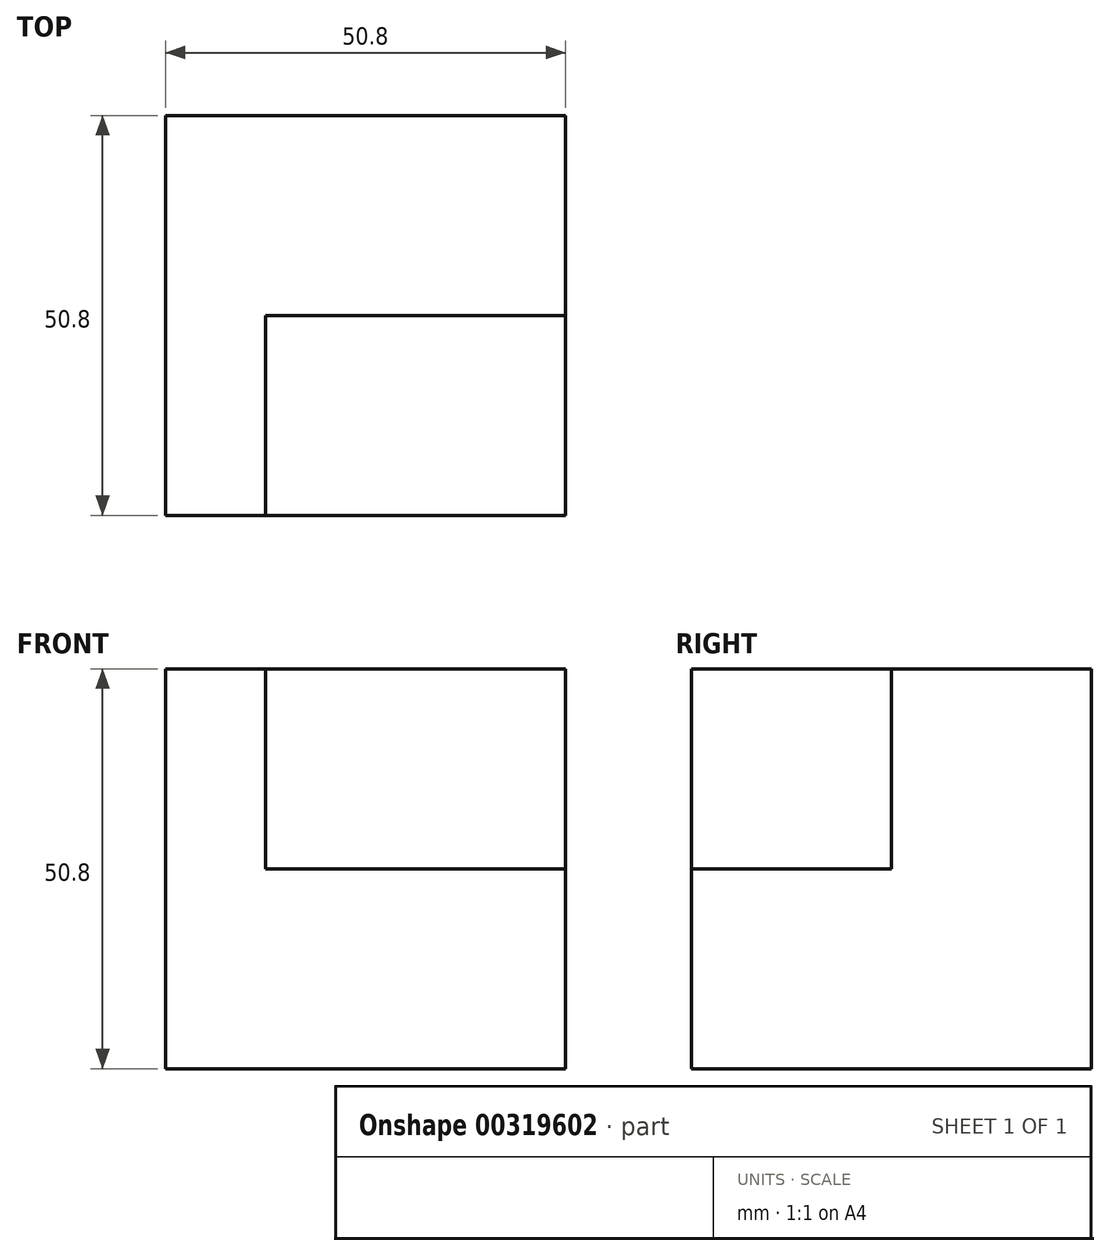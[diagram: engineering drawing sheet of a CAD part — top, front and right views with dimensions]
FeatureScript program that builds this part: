
annotation { "Feature Type Name" : "Feature", "Feature Type Description" : "" }
export const myFeature = defineFeature(function(context is Context, id is Id, definition is map)
    precondition{}
    {
        {
            var Q0;
            Q0=qCreatedBy(makeId("Front.planeOp"),FACE);
            var sketch = newSketch(context, id + "F0", { "sketchPlane" : qUnion([Q0])});
            skLineSegment(sketch, "E0.bottom", {"start": v(-36.56, 56.22) * mm, "end": v(14.24, 56.22) * mm});
            skLineSegment(sketch, "E0.top", {"start": v(-36.56, 5.42) * mm, "end": v(14.24, 5.42) * mm});
            skLineSegment(sketch, "E0.left", {"start": v(-36.56, 56.22) * mm, "end": v(-36.56, 5.42) * mm});
            skLineSegment(sketch, "E0.right", {"start": v(14.24, 56.22) * mm, "end": v(14.24, 5.42) * mm});
            skSolve(sketch);
        }
        {
            var Q0;
            Q0=makeQuery(id+"F0.imprint","IMPRINT",FACE,{"disambiguationData":[TD([[makeQuery(id+"F0.imprint","IMPRINT",EDGE,{"derivedFrom":sQuery(id+"F0.wireOp",EDGE,"E0.bottom")}),-1.0]])]});
            extrude(context, id + "F1", {"entities" : qUnion([Q0]), "depth" : 50.8 * mm});
        }
        {
            var Q0;
            Q0=makeQuery(id+"F1.opExtrude","CAP_FACE",FACE,{"disambiguationData":[OSD([sQuery(id+"F0.wireOp",EDGE,"E0.bottom"),sQuery(id+"F0.wireOp",EDGE,"E0.top"),sQuery(id+"F0.wireOp",EDGE,"E0.left"),sQuery(id+"F0.wireOp",EDGE,"E0.right")])],"isStart":false});
            var sketch = newSketch(context, id + "F2", { "sketchPlane" : qUnion([Q0])});
            skLineSegment(sketch, "E1", {"start": v(-36.56, 56.22) * mm, "end": v(-23.86, 56.22) * mm});
            skLineSegment(sketch, "E2", {"start": v(-23.86, 56.22) * mm, "end": v(-23.86, 30.82) * mm});
            skLineSegment(sketch, "E3", {"start": v(-23.86, 30.82) * mm, "end": v(14.24, 30.82) * mm});
            skLineSegment(sketch, "E4", {"start": v(14.24, 30.82) * mm, "end": v(14.24, 56.22) * mm});
            skLineSegment(sketch, "E5", {"start": v(14.24, 56.22) * mm, "end": v(-23.86, 56.22) * mm});
            skSolve(sketch);
        }
        {
            var Q0;
            Q0 = qSketchRegion(id + "F2", true);
            extrude(context, id + "F3", {"entities" : qUnion([Q0]), "operationType" : NewBodyOperationType.REMOVE, "oppositeDirection" : true, "depth" : 25.4 * mm});
        }
    });
